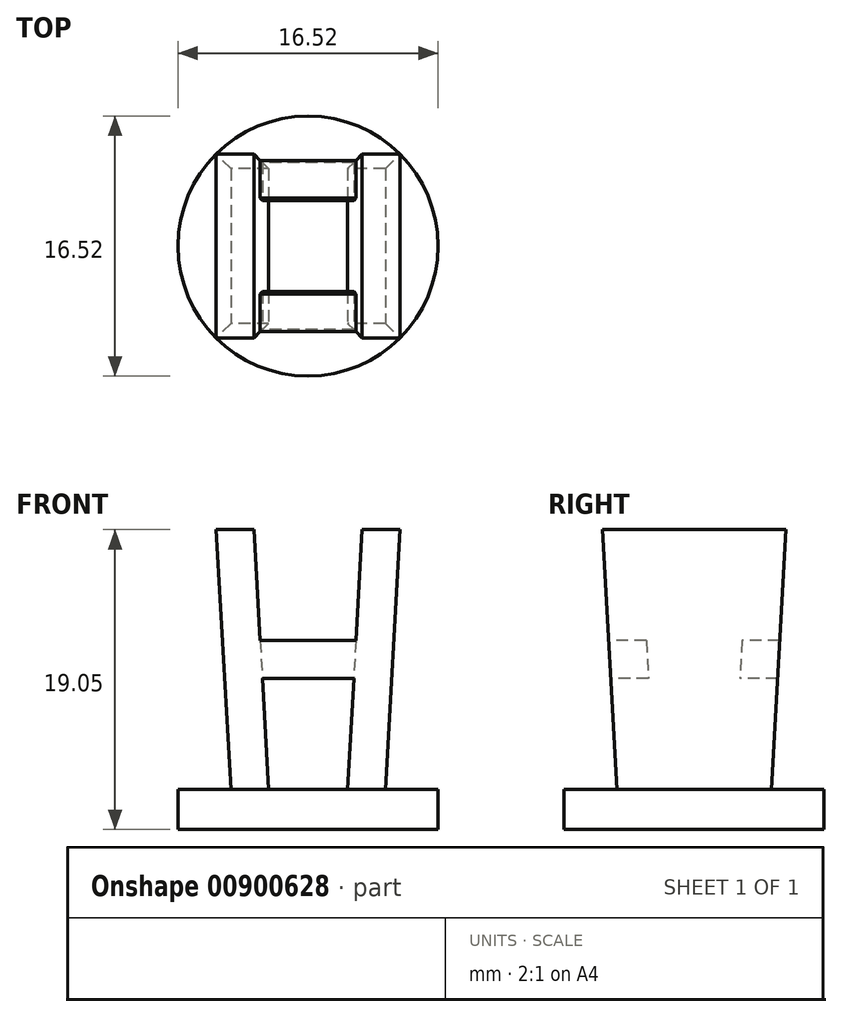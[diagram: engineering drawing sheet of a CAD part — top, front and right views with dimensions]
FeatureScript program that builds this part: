
annotation { "Feature Type Name" : "Feature", "Feature Type Description" : "" }
export const myFeature = defineFeature(function(context is Context, id is Id, definition is map)
    precondition{}
    {
        {
            var Q0;
            Q0=qCreatedBy(makeId("Top.planeOp"),FACE);
            var sketch = newSketch(context, id + "F0", { "sketchPlane" : qUnion([Q0])});
            skCircle(sketch, "E0", {"center": v(0, 0) * mm, "radius": 8.26 * mm});
            skSolve(sketch);
        }
        {
            var Q0;
            Q0 = qSketchRegion(id + "F0", true);
            extrude(context, id + "F1", {"entities" : qUnion([Q0]), "depth" : 2.54 * mm, "offsetDistance" : 25.4 * mm});
        }
        {
            var Q0;
            Q0=qCreatedBy(makeId("Top.planeOp"),FACE);
            var sketch = newSketch(context, id + "F2", { "sketchPlane" : qUnion([Q0])});
            skLineSegment(sketch, "E1.bottom", {"start": v(4.76, 4.76) * mm, "end": v(-4.76, 4.76) * mm});
            skLineSegment(sketch, "E1.top", {"start": v(4.76, -4.76) * mm, "end": v(-4.76, -4.76) * mm});
            skLineSegment(sketch, "E1.left", {"start": v(4.76, 4.76) * mm, "end": v(4.76, -4.76) * mm});
            skLineSegment(sketch, "E1.right", {"start": v(-4.76, 4.76) * mm, "end": v(-4.76, -4.76) * mm});
            skPoint(sketch, "E1.middle", {"position": v(0, 0) * mm});
            skLineSegment(sketch, "E2.bottom", {"start": v(-4.76, 4.76) * mm, "end": v(-2.36, 4.76) * mm});
            skLineSegment(sketch, "E2.top", {"start": v(-4.76, 2.36) * mm, "end": v(-2.36, 2.36) * mm});
            skLineSegment(sketch, "E2.left", {"start": v(-4.76, 4.76) * mm, "end": v(-4.76, 2.36) * mm});
            skLineSegment(sketch, "E2.right", {"start": v(-2.36, 4.76) * mm, "end": v(-2.36, 2.36) * mm, "construction": true});
            skLineSegment(sketch, "E3.bottom", {"start": v(4.76, 4.76) * mm, "end": v(2.36, 4.76) * mm});
            skLineSegment(sketch, "E3.top", {"start": v(4.76, 2.36) * mm, "end": v(2.36, 2.36) * mm, "construction": true});
            skLineSegment(sketch, "E3.left", {"start": v(4.76, 4.76) * mm, "end": v(4.76, 2.36) * mm});
            skLineSegment(sketch, "E3.right", {"start": v(2.36, 4.76) * mm, "end": v(2.36, 2.36) * mm, "construction": true});
            skLineSegment(sketch, "E4.bottom", {"start": v(4.76, -4.76) * mm, "end": v(2.36, -4.76) * mm});
            skLineSegment(sketch, "E4.top", {"start": v(4.76, -2.36) * mm, "end": v(2.36, -2.36) * mm, "construction": true});
            skLineSegment(sketch, "E4.left", {"start": v(4.76, -4.76) * mm, "end": v(4.76, -2.36) * mm});
            skLineSegment(sketch, "E4.right", {"start": v(2.36, -4.76) * mm, "end": v(2.36, -2.36) * mm, "construction": true});
            skLineSegment(sketch, "E5.bottom", {"start": v(-4.76, -4.76) * mm, "end": v(-2.36, -4.76) * mm});
            skLineSegment(sketch, "E5.top", {"start": v(-4.76, -2.36) * mm, "end": v(-2.36, -2.36) * mm, "construction": true});
            skLineSegment(sketch, "E5.left", {"start": v(-4.76, -4.76) * mm, "end": v(-4.76, -2.36) * mm});
            skLineSegment(sketch, "E5.right", {"start": v(-2.36, -4.76) * mm, "end": v(-2.36, -2.36) * mm, "construction": true});
            skSolve(sketch);
        }
        {
            var Q0;
            Q0=qCreatedBy(makeId("Top.planeOp"),FACE);
            cPlane(context, id + "F3", {"entities" : qUnion([Q0]), "cplaneType" : CPlaneType.OFFSET, "offset" : 19.05 * mm, "width" : 152.4 * mm, "height" : 152.4 * mm});
        }
        {
            var Q0;
            Q0=qCreatedBy(id+"F3.planeOp",FACE);
            var sketch = newSketch(context, id + "F4", { "sketchPlane" : qUnion([Q0])});
            skLineSegment(sketch, "E6.bottom", {"start": v(-5.84, 5.84) * mm, "end": v(5.84, 5.84) * mm});
            skLineSegment(sketch, "E6.top", {"start": v(-5.84, -5.84) * mm, "end": v(5.84, -5.84) * mm});
            skLineSegment(sketch, "E6.left", {"start": v(-5.84, 5.84) * mm, "end": v(-5.84, -5.84) * mm});
            skLineSegment(sketch, "E6.right", {"start": v(5.84, 5.84) * mm, "end": v(5.84, -5.84) * mm});
            skPoint(sketch, "E6.middle", {"position": v(0, 0) * mm});
            skLineSegment(sketch, "E7.bottom", {"start": v(-5.84, 5.84) * mm, "end": v(-3.44, 5.84) * mm});
            skLineSegment(sketch, "E7.top", {"start": v(-5.84, 3.44) * mm, "end": v(-3.44, 3.44) * mm, "construction": true});
            skLineSegment(sketch, "E7.left", {"start": v(-5.84, 5.84) * mm, "end": v(-5.84, 3.44) * mm});
            skLineSegment(sketch, "E7.right", {"start": v(-3.44, 5.84) * mm, "end": v(-3.44, 3.44) * mm, "construction": true});
            skLineSegment(sketch, "E8.bottom", {"start": v(5.84, 5.84) * mm, "end": v(3.44, 5.84) * mm});
            skLineSegment(sketch, "E8.top", {"start": v(5.84, 3.44) * mm, "end": v(3.44, 3.44) * mm, "construction": true});
            skLineSegment(sketch, "E8.left", {"start": v(5.84, 5.84) * mm, "end": v(5.84, 3.44) * mm});
            skLineSegment(sketch, "E8.right", {"start": v(3.44, 5.84) * mm, "end": v(3.44, 3.44) * mm, "construction": true});
            skLineSegment(sketch, "E9.bottom", {"start": v(5.84, -5.84) * mm, "end": v(3.44, -5.84) * mm});
            skLineSegment(sketch, "E9.top", {"start": v(5.84, -3.44) * mm, "end": v(3.44, -3.44) * mm, "construction": true});
            skLineSegment(sketch, "E9.left", {"start": v(5.84, -5.84) * mm, "end": v(5.84, -3.44) * mm});
            skLineSegment(sketch, "E9.right", {"start": v(3.44, -5.84) * mm, "end": v(3.44, -3.44) * mm, "construction": true});
            skLineSegment(sketch, "E10.bottom", {"start": v(-5.84, -5.84) * mm, "end": v(-3.44, -5.84) * mm});
            skLineSegment(sketch, "E10.top", {"start": v(-5.84, -3.44) * mm, "end": v(-3.44, -3.44) * mm, "construction": true});
            skLineSegment(sketch, "E10.left", {"start": v(-5.84, -5.84) * mm, "end": v(-5.84, -3.44) * mm});
            skLineSegment(sketch, "E10.right", {"start": v(-3.44, -5.84) * mm, "end": v(-3.44, -3.44) * mm, "construction": true});
            skSolve(sketch);
        }
        {
            var Q1;
            Q1=makeQuery(id+"F2.imprint","IMPRINT",FACE,{"disambiguationData":[TD([[makeQuery(id+"F2.imprint","IMPRINT",EDGE,{"derivedFrom":sQuery(id+"F2.wireOp",EDGE,"E1.bottom")}),1.0]])]});
            var Q2;
            Q2=makeQuery(id+"F4.imprint","IMPRINT",FACE,{"disambiguationData":[TD([[makeQuery(id+"F4.imprint","IMPRINT",EDGE,{"derivedFrom":sQuery(id+"F4.wireOp",EDGE,"E6.bottom")}),-1.0]])]});
            loft(context, id + "F5", {"operationType" : NewBodyOperationType.ADD, "sheetProfilesArray" : [{ "sheetProfileEntities" : qUnion([Q1]) }, { "sheetProfileEntities" : qUnion([Q2]) }]});
        }
        {
            var Q0;
            Q0=qCreatedBy(makeId("Front.planeOp"),FACE);
            cPlane(context, id + "F6", {"entities" : qUnion([Q0]), "cplaneType" : CPlaneType.OFFSET, "offset" : 25.4 * mm, "width" : 152.4 * mm, "height" : 152.4 * mm});
        }
        {
            var Q0;
            Q0=qCreatedBy(id+"F6.planeOp",FACE);
            var sketch = newSketch(context, id + "F7", { "sketchPlane" : qUnion([Q0])});
            skLineSegment(sketch, "E11.0", {"start": v(4.9, 2.54) * mm, "end": v(5.84, 19.05) * mm});
            skLineSegment(sketch, "E11.1", {"start": v(-4.9, 2.54) * mm, "end": v(-5.84, 19.05) * mm});
            skLineSegment(sketch, "E11.2", {"start": v(4.9, 2.54) * mm, "end": v(-4.9, 2.54) * mm});
            skLineSegment(sketch, "E11.3", {"start": v(-5.84, 19.05) * mm, "end": v(5.84, 19.05) * mm});
            skLineSegment(sketch, "E12", {"start": v(3.44, 19.05) * mm, "end": v(2.5, 2.54) * mm});
            skLineSegment(sketch, "E13", {"start": v(-3.44, 19.05) * mm, "end": v(-2.5, 2.54) * mm});
            skLineSegment(sketch, "E14", {"start": v(5.37, 10.8) * mm, "end": v(-5.37, 10.8) * mm, "construction": true});
            skLineSegment(sketch, "E15", {"start": v(3.04, 12) * mm, "end": v(-3.04, 12) * mm});
            skLineSegment(sketch, "E16", {"start": v(-2.9, 9.6) * mm, "end": v(2.9, 9.6) * mm});
            skLineSegment(sketch, "E17", {"start": v(0, 12) * mm, "end": v(0, 9.6) * mm, "construction": true});
            skPoint(sketch, "E18", {"position": v(0, 10.8) * mm});
            skSolve(sketch);
        }
        {
            var Q0;
            {var subQ5=sQuery(id+"F7.wireOp",EDGE,"E15");Q0=makeQuery(id+"F7.imprint","IMPRINT",FACE,{"disambiguationData":[TD([[makeQuery(id+"F7.imprint","IMPRINT",EDGE,{"derivedFrom":subQ5}),-1.0]])]});}
            var Q1;
            {var subQ5=sQuery(id+"F7.wireOp",EDGE,"E16");Q1=makeQuery(id+"F7.imprint","IMPRINT",FACE,{"disambiguationData":[TD([[makeQuery(id+"F7.imprint","IMPRINT",EDGE,{"derivedFrom":subQ5}),-1.0]])]});}
            extrude(context, id + "F8", {"entities" : qUnion([Q0, Q1]), "operationType" : NewBodyOperationType.REMOVE, "endBound" : BoundingType.THROUGH_ALL, "oppositeDirection" : true, "depth" : 25.4 * mm, "offsetDistance" : 25.4 * mm});
        }
        {
            var Q0;
            {var subQ0=sQuery(id+"F7.wireOp",EDGE,"E15");Q0=makeQuery(id+"FSzBBtu7wnrdoTO_1.1.F8.boolean.opBoolean","MERGE",FACE,{"derivedFrom":[makeQuery(id+"F8.boolean.opBoolean","COPY",FACE,{"derivedFrom":makeQuery(id+"F8.opExtrude","SWEPT_FACE",FACE,{"disambiguationData":[OSD([subQ0])]})})],"fromTools":[makeQuery(id+"FSzBBtu7wnrdoTO_1.1.F8.opExtrude","SWEPT_FACE",FACE,{"disambiguationData":[OSD([subQ0])]})]});}
            var sketch = newSketch(context, id + "F9", { "sketchPlane" : qUnion([Q0])});
            skLineSegment(sketch, "E19.bottom", {"start": v(-3.04, 3.04) * mm, "end": v(3.04, 3.04) * mm});
            skLineSegment(sketch, "E19.top", {"start": v(-3.04, -3.04) * mm, "end": v(3.04, -3.04) * mm});
            skLineSegment(sketch, "E19.left", {"start": v(-3.04, 3.04) * mm, "end": v(-3.04, -3.04) * mm});
            skLineSegment(sketch, "E19.right", {"start": v(3.04, 3.04) * mm, "end": v(3.04, -3.04) * mm});
            skSolve(sketch);
        }
        {
            var Q0;
            {var subQ0=sQuery(id+"F7.wireOp",EDGE,"E16");Q0=makeQuery(id+"FSzBBtu7wnrdoTO_1.1.F8.boolean.opBoolean","MERGE",FACE,{"derivedFrom":[makeQuery(id+"F8.boolean.opBoolean","COPY",FACE,{"derivedFrom":makeQuery(id+"F8.opExtrude","SWEPT_FACE",FACE,{"disambiguationData":[OSD([subQ0])]})})],"fromTools":[makeQuery(id+"FSzBBtu7wnrdoTO_1.1.F8.opExtrude","SWEPT_FACE",FACE,{"disambiguationData":[OSD([subQ0])]})]});}
            var sketch = newSketch(context, id + "F10", { "sketchPlane" : qUnion([Q0])});
            skLineSegment(sketch, "E20.bottom", {"start": v(-2.9, 2.9) * mm, "end": v(2.9, 2.9) * mm});
            skLineSegment(sketch, "E20.top", {"start": v(-2.9, -2.9) * mm, "end": v(2.9, -2.9) * mm});
            skLineSegment(sketch, "E20.left", {"start": v(-2.9, 2.9) * mm, "end": v(-2.9, -2.9) * mm});
            skLineSegment(sketch, "E20.right", {"start": v(2.9, 2.9) * mm, "end": v(2.9, -2.9) * mm});
            skSolve(sketch);
        }
        {
            var Q1;
            Q1 = qSketchRegion(id + "F9", true);
            var Q2;
            Q2 = qSketchRegion(id + "F10", true);
            loft(context, id + "F11", {"operationType" : NewBodyOperationType.REMOVE, "sheetProfilesArray" : [{ "sheetProfileEntities" : qUnion([Q1]) }, { "sheetProfileEntities" : qUnion([Q2]) }]});
        }
    });
